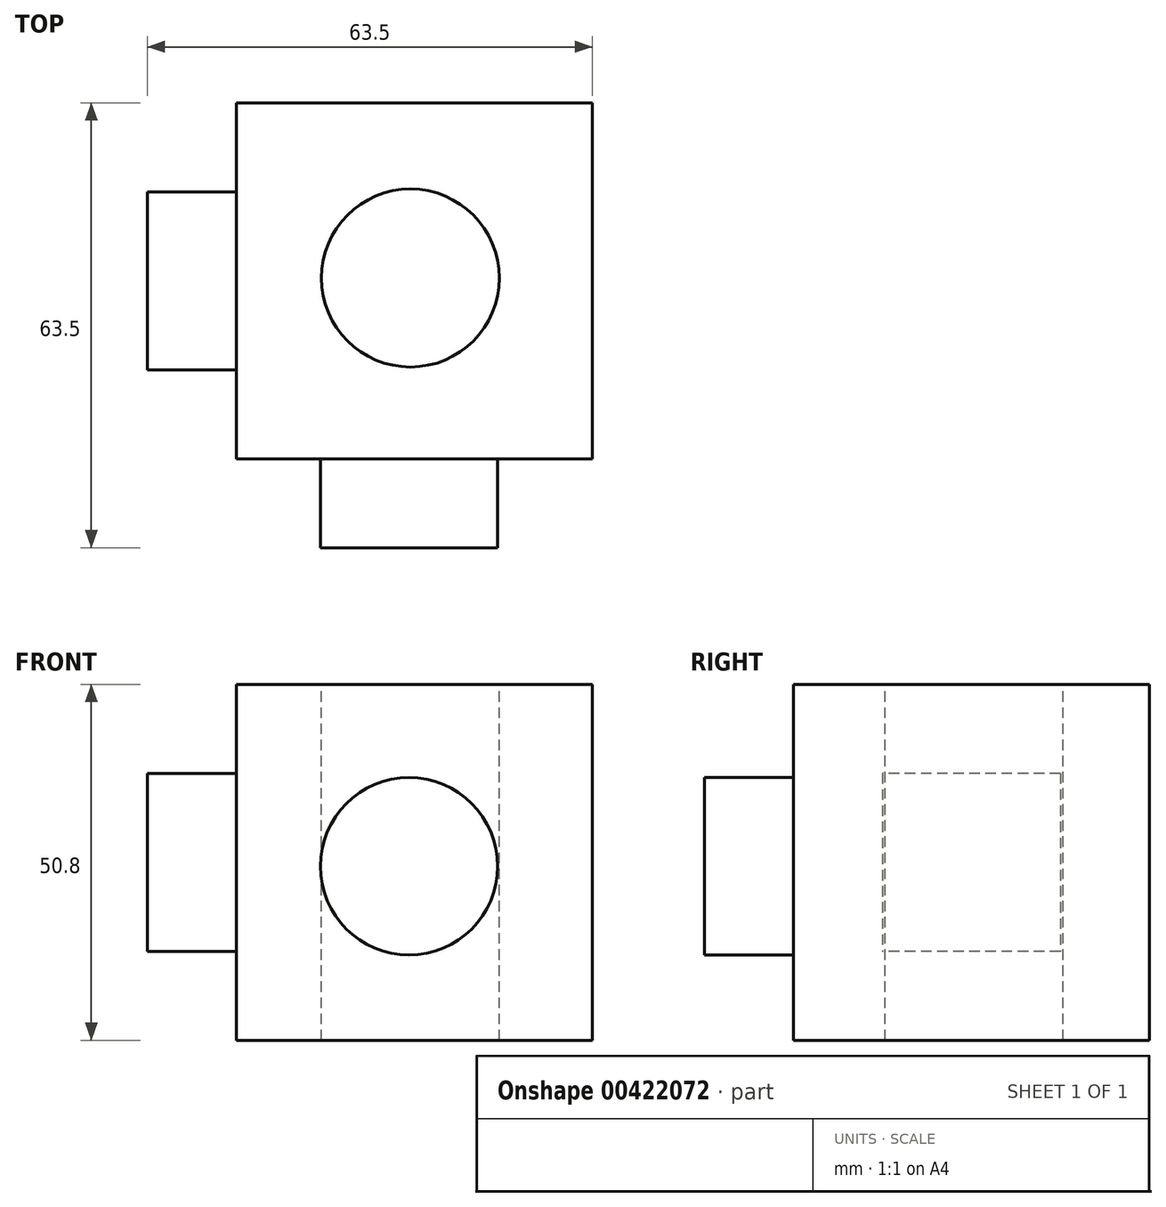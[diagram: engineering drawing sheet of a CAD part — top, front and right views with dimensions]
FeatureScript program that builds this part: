
annotation { "Feature Type Name" : "Feature", "Feature Type Description" : "" }
export const myFeature = defineFeature(function(context is Context, id is Id, definition is map)
    precondition{}
    {
        {
            var Q0;
            Q0=qCreatedBy(makeId("Front.planeOp"),FACE);
            var sketch = newSketch(context, id + "F0", { "sketchPlane" : qUnion([Q0])});
            skLineSegment(sketch, "E0.bottom", {"start": v(0, 0) * mm, "end": v(-50.8, 0) * mm});
            skLineSegment(sketch, "E0.top", {"start": v(0, 50.8) * mm, "end": v(-50.8, 50.8) * mm});
            skLineSegment(sketch, "E0.left", {"start": v(0, 0) * mm, "end": v(0, 50.8) * mm});
            skLineSegment(sketch, "E0.right", {"start": v(-50.8, 0) * mm, "end": v(-50.8, 50.8) * mm});
            skSolve(sketch);
        }
        {
            var Q0;
            Q0 = qSketchRegion(id + "F0", true);
            extrude(context, id + "F1", {"entities" : qUnion([Q0]), "depth" : 50.8 * mm});
        }
        {
            var Q0;
            Q0=makeQuery(id+"F1.opExtrude","SWEPT_FACE",FACE,{"disambiguationData":[OSD([sQuery(id+"F0.wireOp",EDGE,"E0.top")])]});
            var sketch = newSketch(context, id + "F2", { "sketchPlane" : qUnion([Q0])});
            skCircle(sketch, "E1", {"center": v(-25.97, -25.02) * mm, "radius": 12.7 * mm});
            skSolve(sketch);
        }
        {
            var Q0;
            Q0 = qSketchRegion(id + "F2", true);
            extrude(context, id + "F3", {"entities" : qUnion([Q0]), "operationType" : NewBodyOperationType.REMOVE, "oppositeDirection" : true, "depth" : 50.8 * mm});
        }
        {
            var Q0;
            Q0=makeQuery(id+"F1.opExtrude","CAP_FACE",FACE,{"disambiguationData":[OSD([sQuery(id+"F0.wireOp",EDGE,"E0.bottom"),sQuery(id+"F0.wireOp",EDGE,"E0.top"),sQuery(id+"F0.wireOp",EDGE,"E0.left"),sQuery(id+"F0.wireOp",EDGE,"E0.right")])],"isStart":false});
            var sketch = newSketch(context, id + "F4", { "sketchPlane" : qUnion([Q0])});
            skCircle(sketch, "E2", {"center": v(-26.16, 24.82) * mm, "radius": 12.66 * mm});
            skSolve(sketch);
        }
        {
            var Q0;
            Q0 = qSketchRegion(id + "F4", true);
            extrude(context, id + "F5", {"entities" : qUnion([Q0]), "operationType" : NewBodyOperationType.ADD, "depth" : 12.7 * mm});
        }
        {
            var Q0;
            Q0=makeQuery(id+"F1.opExtrude","SWEPT_FACE",FACE,{"disambiguationData":[OSD([sQuery(id+"F0.wireOp",EDGE,"E0.right")])]});
            var sketch = newSketch(context, id + "F6", { "sketchPlane" : qUnion([Q0])});
            skLineSegment(sketch, "E3.bottom", {"start": v(12.7, 38.1) * mm, "end": v(38.1, 38.1) * mm});
            skLineSegment(sketch, "E3.top", {"start": v(12.7, 12.7) * mm, "end": v(38.1, 12.7) * mm});
            skLineSegment(sketch, "E3.left", {"start": v(12.7, 38.1) * mm, "end": v(12.7, 12.7) * mm});
            skLineSegment(sketch, "E3.right", {"start": v(38.1, 38.1) * mm, "end": v(38.1, 12.7) * mm});
            skSolve(sketch);
        }
        {
            var Q0;
            Q0 = qSketchRegion(id + "F6", true);
            extrude(context, id + "F7", {"entities" : qUnion([Q0]), "operationType" : NewBodyOperationType.ADD, "depth" : 12.7 * mm});
        }
    });
